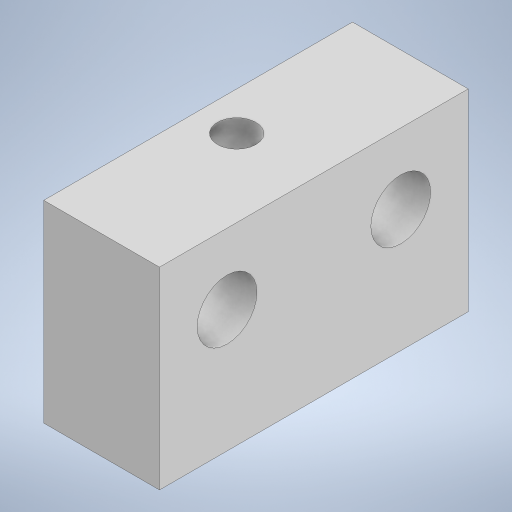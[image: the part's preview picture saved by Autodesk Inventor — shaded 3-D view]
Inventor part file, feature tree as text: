
AUTODESK INVENTOR PART (.ipt)
format: ipt  version: 2024 (Build 280153000, 153)  size: 210,432 bytes
history: native  units: mm
features: sketch x4, extrude x2, sweep x1
ambient origin geometry x8: Origin, YZ Plane, XZ Plane, XY Plane, X Axis, Y Axis, Z Axis, Center Point
bodies: Solid1 (feature_tree)
feature tree (7):
  extrude  "Extrusion1"  Depth=16.0mm
  sweep  "Sweep1"
  extrude  "Extrusion3"  TaperAngle=60.0deg  [1 undecoded]
  sketch  "Sketch1"  dims[d0=6.0mm d1=16.0mm]
  sketch  "Sketch2"  dims[d2=10.0mm d3=0.0mm d4=2.0mm]
  sketch  "Sketch3"  dims[d5=2.0mm d6=60.0deg]
  sketch  "Sketch5"  dims[d7=0.0mm d8=0.0mm d13=3.1mm d14=3.1mm d15=10.0mm d16=0.0mm]
note: 1 required parameter value undecoded (feature->parameter linkage not recoverable at this tier; creation-order binding heuristic only, values carry confidence <= 0.55)
